# Revit family: JAD_RetroColonial_L4433_BIM_DE
name_source: partatom
category: Plumbing Fixtures
revit_build: Autodesk Revit 2015 (Build: 20140606_1530(x64)
units: mm (PartAtom-declared; Revit-internal decimal feet)

## types (1)
- L4433XO - COLONIAL SNK MXR RIM MTD CHROME SL S/SPT
    Accessories = www.idealspec.co.uk
    AreaUnits = millimeters
    Assembly Code = C1030200
    AssetType = Fixed
    BIMObjectName = JAD_Jado_KitchenSinks_RetroColonial_L4433
    BarCode = 5017830262541
    Brand = Ideal Standard
    ConnectionType = Plumbing
    Cost = 0 $
    Description = COLONIAL SNK MXR RIM MTD CHROME SL S/SPT
    DurationUnit = year
    Features = COLONIAL SNK MXR RIM MTD CHROME SL S/SPT
    Help = www.idealstandard.de
    IfcExportAs = IfcValveType
    IfcExportType = KITCHEN MIXERS
    InstallationInstructions = www.idealstandard.de
    LinearUnits = millimeters
    MaintenanceInformation = www.idealstandard.de
    Manufacturer = www.idealstandard.de
    ManufacturerURL = www.idealstandard.de
    Model = L4433XO
    ModelNumber = L4433XO
    ModelReference = COLONIAL SNK MXR RIM MTD CHROME SL S/SPT
    Name = KitchenSinks_RetroColonial_L4433_JAD
    NettWeight = 3,13 KG
    NominalDepth = 420 mm
    NominalHeight = 75 mm
    NominalLength = 420 mm
    NominalWidth = 320 mm
    ProductInformation = www.idealstandard.de
    Shape = Sculptured
    Size = 75 x 420 x 320 mm
    Space = Internal
    SpareParts = www.idealstandard.de
    TestPressure = 10 bar
    URL = www.idealstandard.de
    Uniclass2015Code = Pr_40_20_96_45
    Uniclass2015Title = Kitchen sinks
    Uniclass2015Version = Products v1.1

## geometry (parser evidence)
native form markers: Blend x4
no freeform markers — native parametric forms only
